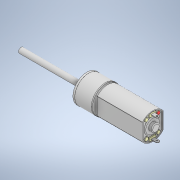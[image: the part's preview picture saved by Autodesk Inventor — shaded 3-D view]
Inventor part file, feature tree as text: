
AUTODESK INVENTOR PART (.ipt)
format: ipt  version: 2020 (Build 240168000, 168)  size: 299,008 bytes
history: native  units: in
note: dims shown in document units (in); Inventor stores cm internally (conversion verified against a paired STEP export)
features: other x3, extrude x1
ambient origin geometry x8: Origin, YZ Plane, XZ Plane, XY Plane, X Axis, Y Axis, Z Axis, Center Point
bodies: Solid1 (feature_tree), Solid2 (feature_tree), Solid3 (feature_tree), Solid4 (feature_tree)
feature tree (4):
  other  "Cut-Extrude1"
  other  "Cut-Extrude5[1]"
  other  "Cut-Extrude5[2]"
  extrude  "Extrude13"  [1 undecoded]
note: 1 required parameter value undecoded (feature->parameter linkage not recoverable at this tier; creation-order binding heuristic only, values carry confidence <= 0.55)
